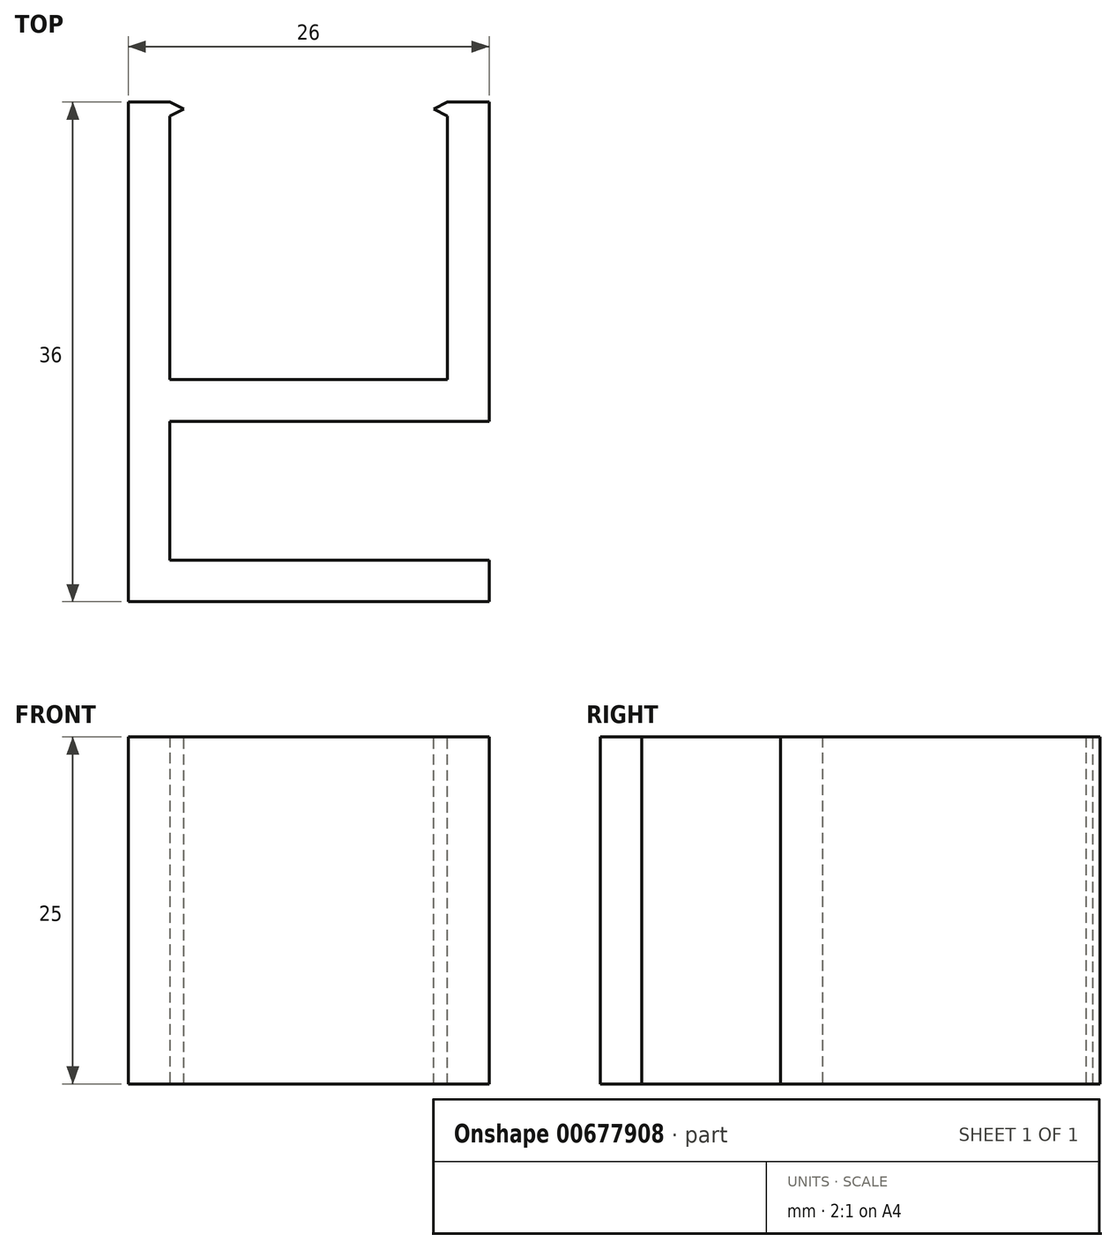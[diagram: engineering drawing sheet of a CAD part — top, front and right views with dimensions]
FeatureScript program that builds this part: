
annotation { "Feature Type Name" : "Feature", "Feature Type Description" : "" }
export const myFeature = defineFeature(function(context is Context, id is Id, definition is map)
    precondition{}
    {
        {
            var Q0;
            Q0=qCreatedBy(makeId("Top.planeOp"),FACE);
            var sketch = newSketch(context, id + "F0", { "sketchPlane" : qUnion([Q0])});
            skLineSegment(sketch, "E0.bottom", {"start": v(-15.6, 12.18) * mm, "end": v(-12.6, 12.18) * mm});
            skLineSegment(sketch, "E0.top", {"start": v(-15.6, -10.82) * mm, "end": v(-12.6, -10.82) * mm});
            skLineSegment(sketch, "E0.left", {"start": v(-15.6, 12.18) * mm, "end": v(-15.6, -10.82) * mm});
            skLineSegment(sketch, "E0.right", {"start": v(-12.6, 12.18) * mm, "end": v(-12.6, -10.82) * mm});
            skLineSegment(sketch, "E1.bottom", {"start": v(-12.6, -10.82) * mm, "end": v(7.4, -10.82) * mm});
            skLineSegment(sketch, "E1.top", {"start": v(-12.6, -7.82) * mm, "end": v(7.4, -7.82) * mm});
            skLineSegment(sketch, "E1.left", {"start": v(-12.6, -10.82) * mm, "end": v(-12.6, -7.82) * mm});
            skLineSegment(sketch, "E1.right", {"start": v(7.4, -10.82) * mm, "end": v(7.4, -7.82) * mm});
            skLineSegment(sketch, "E2.bottom", {"start": v(7.4, -10.82) * mm, "end": v(10.4, -10.82) * mm});
            skLineSegment(sketch, "E2.top", {"start": v(7.4, 12.18) * mm, "end": v(10.4, 12.18) * mm});
            skLineSegment(sketch, "E2.left", {"start": v(7.4, -10.82) * mm, "end": v(7.4, 12.18) * mm});
            skLineSegment(sketch, "E2.right", {"start": v(10.4, -10.82) * mm, "end": v(10.4, 12.18) * mm});
            skLineSegment(sketch, "E3.bottom", {"start": v(-12.6, 12.18) * mm, "end": v(-11.6, 12.18) * mm});
            skLineSegment(sketch, "E3.top", {"start": v(-12.6, 11.18) * mm, "end": v(-11.6, 11.18) * mm});
            skLineSegment(sketch, "E3.left", {"start": v(-12.6, 12.18) * mm, "end": v(-12.6, 11.18) * mm});
            skLineSegment(sketch, "E3.right", {"start": v(-11.6, 12.18) * mm, "end": v(-11.6, 11.18) * mm});
            skLineSegment(sketch, "E4.bottom", {"start": v(7.4, 12.18) * mm, "end": v(6.4, 12.18) * mm});
            skLineSegment(sketch, "E4.top", {"start": v(7.4, 11.18) * mm, "end": v(6.4, 11.18) * mm});
            skLineSegment(sketch, "E4.left", {"start": v(7.4, 12.18) * mm, "end": v(7.4, 11.18) * mm});
            skLineSegment(sketch, "E4.right", {"start": v(6.4, 12.18) * mm, "end": v(6.4, 11.18) * mm});
            skLineSegment(sketch, "E5.top", {"start": v(-15.6, -20.82) * mm, "end": v(-12.6, -20.82) * mm});
            skLineSegment(sketch, "E5.left", {"start": v(-15.6, -10.82) * mm, "end": v(-15.6, -20.82) * mm});
            skLineSegment(sketch, "E5.right", {"start": v(-12.6, -10.82) * mm, "end": v(-12.6, -20.82) * mm});
            skLineSegment(sketch, "E6.bottom", {"start": v(-15.6, -20.82) * mm, "end": v(10.4, -20.82) * mm});
            skLineSegment(sketch, "E6.top", {"start": v(-15.6, -23.82) * mm, "end": v(10.4, -23.82) * mm});
            skLineSegment(sketch, "E6.left", {"start": v(-15.6, -20.82) * mm, "end": v(-15.6, -23.82) * mm});
            skLineSegment(sketch, "E6.right", {"start": v(10.4, -20.82) * mm, "end": v(10.4, -23.82) * mm});
            skSolve(sketch);
        }
        {
            var Q0;
            Q0=makeQuery(id+"F0.imprint","IMPRINT",FACE,{"disambiguationData":[TD([[makeQuery(id+"F0.imprint","IMPRINT",EDGE,{"derivedFrom":sQuery(id+"F0.wireOp",EDGE,"E0.bottom")}),-1.0]])]});
            var Q1;
            Q1=makeQuery(id+"F0.imprint","IMPRINT",FACE,{"disambiguationData":[TD([[makeQuery(id+"F0.imprint","IMPRINT",EDGE,{"derivedFrom":sQuery(id+"F0.wireOp",EDGE,"E3.bottom")}),-1.0]])]});
            var Q2;
            {var subQ0=sQuery(id+"F0.wireOp",EDGE,"E1.bottom");Q2=makeQuery(id+"F0.imprint","IMPRINT",FACE,{"disambiguationData":[TD([[makeQuery(id+"F0.imprint","IMPRINT",EDGE,{"derivedFrom":subQ0}),1.0]])]});}
            var Q3;
            {var subQ3=sQuery(id+"F0.wireOp",EDGE,"E2.bottom");Q3=makeQuery(id+"F0.imprint","IMPRINT",FACE,{"disambiguationData":[TD([[makeQuery(id+"F0.imprint","IMPRINT",EDGE,{"derivedFrom":subQ3}),1.0]])]});}
            var Q4;
            Q4=makeQuery(id+"F0.imprint","IMPRINT",FACE,{"disambiguationData":[TD([[makeQuery(id+"F0.imprint","IMPRINT",EDGE,{"derivedFrom":sQuery(id+"F0.wireOp",EDGE,"E0.top")}),-1.0]])]});
            var Q5;
            Q5=makeQuery(id+"F0.imprint","IMPRINT",FACE,{"disambiguationData":[TD([[makeQuery(id+"F0.imprint","IMPRINT",EDGE,{"derivedFrom":sQuery(id+"F0.wireOp",EDGE,"E6.top")}),1.0]])]});
            var Q6;
            Q6=makeQuery(id+"F0.imprint","IMPRINT",FACE,{"disambiguationData":[TD([[makeQuery(id+"F0.imprint","IMPRINT",EDGE,{"derivedFrom":sQuery(id+"F0.wireOp",EDGE,"E4.bottom")}),1.0]])]});
            extrude(context, id + "F1", {"entities" : qUnion([Q0, Q1, Q2, Q3, Q4, Q5, Q6]), "depth" : 25 * mm, "offsetDistance" : 25 * mm});
        }
        {
            var Q0;
            Q0=makeQuery(id+"F1.opExtrude","SWEPT_EDGE",EDGE,{"disambiguationData":[OSD([sQuery(id+"F0.wireOp",EDGE,"E4.top"),sQuery(id+"F0.wireOp",EDGE,"E4.right")])]});
            var Q1;
            Q1=makeQuery(id+"F1.opExtrude","SWEPT_EDGE",EDGE,{"disambiguationData":[OSD([sQuery(id+"F0.wireOp",EDGE,"E3.bottom"),sQuery(id+"F0.wireOp",EDGE,"E3.right")])]});
            chamfer(context, id + "F2", {"entities" : qUnion([Q0, Q1]), "chamferType" : ChamferType.TWO_OFFSETS, "width1" : 1 * mm, "oppositeDirection" : false, "width2" : .5 * mm, "tangentPropagation" : true});
        }
        {
            var Q0;
            Q0=makeQuery(id+"F1.opExtrude","SWEPT_EDGE",EDGE,{"disambiguationData":[OSD([sQuery(id+"F0.wireOp",EDGE,"E4.bottom"),sQuery(id+"F0.wireOp",EDGE,"E4.right")])]});
            var Q1;
            Q1=makeQuery(id+"F1.opExtrude","SWEPT_EDGE",EDGE,{"disambiguationData":[OSD([sQuery(id+"F0.wireOp",EDGE,"E3.top"),sQuery(id+"F0.wireOp",EDGE,"E3.right")])]});
            chamfer(context, id + "F3", {"entities" : qUnion([Q0, Q1]), "chamferType" : ChamferType.TWO_OFFSETS, "width1" : .5 * mm, "oppositeDirection" : false, "width2" : 1 * mm, "tangentPropagation" : true});
        }
    });
